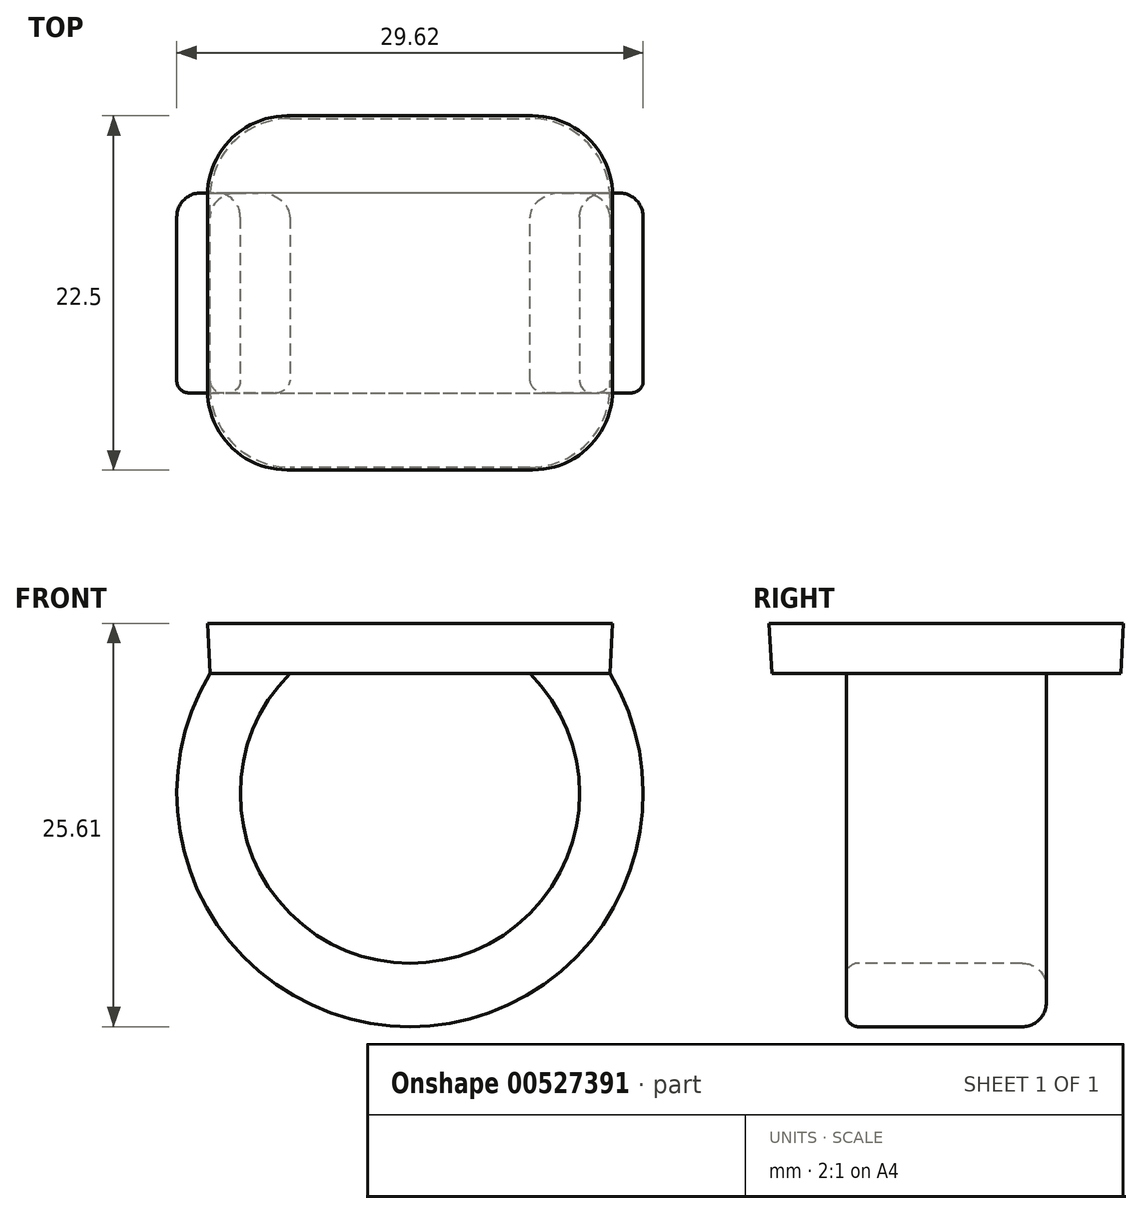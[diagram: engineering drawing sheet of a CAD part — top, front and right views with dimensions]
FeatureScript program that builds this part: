
annotation { "Feature Type Name" : "Feature", "Feature Type Description" : "" }
export const myFeature = defineFeature(function(context is Context, id is Id, definition is map)
    precondition{}
    {
        {
            var Q0;
            Q0=qCreatedBy(makeId("Top.planeOp"),FACE);
            var sketch = newSketch(context, id + "F0", { "sketchPlane" : qUnion([Q0])});
            skLineSegment(sketch, "E0.bottom", {"start": v(-12.7, 11.08) * mm, "end": v(12.7, 11.08) * mm});
            skLineSegment(sketch, "E0.top", {"start": v(-12.7, -11.08) * mm, "end": v(12.7, -11.08) * mm});
            skLineSegment(sketch, "E0.left", {"start": v(-12.7, 11.08) * mm, "end": v(-12.7, -11.08) * mm});
            skLineSegment(sketch, "E0.right", {"start": v(12.7, 11.08) * mm, "end": v(12.7, -11.08) * mm});
            skPoint(sketch, "E0.middle", {"position": v(0, 0) * mm});
            skLineSegment(sketch, "E1.left", {"start": v(23.14, -11.08) * mm, "end": v(23.14, -11.08) * mm});
            skLineSegment(sketch, "E1.right", {"start": v(2.26, -11.08) * mm, "end": v(2.26, -11.08) * mm});
            skPoint(sketch, "E1.middle", {"position": v(12.7, -11.08) * mm});
            skSolve(sketch);
        }
        {
            var Q0;
            Q0 = qSketchRegion(id + "F0", true);
            extrude(context, id + "F1", {"entities" : qUnion([Q0]), "depth" : 3.17 * mm, "offsetDistance" : 25.4 * mm, "hasDraft" : true, "draftAngle" : 3 * degree});
        }
        {
            var Q0;
            Q0=qCreatedBy(makeId("Front.planeOp"),FACE);
            var sketch = newSketch(context, id + "F2", { "sketchPlane" : qUnion([Q0])});
            skArc(sketch, "E2", {"start": v(-10.16, 0) * mm, "mid": v(0, -20.32) * mm, "end": v(10.16, 0) * mm});
            skSolve(sketch);
        }
        {
            var Q0;
            Q0=makeQuery(id+"F1.opExtrude","CAP_FACE",FACE,{"disambiguationData":[OSD([sQuery(id+"F0.wireOp",EDGE,"E0.bottom"),sQuery(id+"F0.wireOp",EDGE,"E0.top"),sQuery(id+"F0.wireOp",EDGE,"E0.left"),sQuery(id+"F0.wireOp",EDGE,"E0.right")])],"isStart":true});
            var sketch = newSketch(context, id + "F3", { "sketchPlane" : qUnion([Q0])});
            skLineSegment(sketch, "E3.bottom", {"start": v(-7.62, -6.35) * mm, "end": v(-12.7, -6.35) * mm});
            skLineSegment(sketch, "E3.top", {"start": v(-7.62, 6.35) * mm, "end": v(-12.7, 6.35) * mm});
            skLineSegment(sketch, "E3.left", {"start": v(-7.62, -6.35) * mm, "end": v(-7.62, 6.35) * mm});
            skLineSegment(sketch, "E3.right", {"start": v(-12.7, -6.35) * mm, "end": v(-12.7, 6.35) * mm});
            skPoint(sketch, "E3.middle", {"position": v(-10.16, 0) * mm});
            skSolve(sketch);
        }
        {
            var Q0;
            Q0 = qSketchRegion(id + "F3", true);
            var Q1;
            Q1 = qConstructionFilter(qBodyType(qCreatedBy(id + "F2" ,EDGE), BodyType.WIRE), ConstructionObject.NO);
            sweep(context, id + "F4", {"operationType" : NewBodyOperationType.ADD, "profiles" : qUnion([Q0]), "path" : qUnion([Q1])});
        }
        {
            var Q0;
            Q0=qCreatedBy(makeId("Front.planeOp"),FACE);
            var sketch = newSketch(context, id + "F5", { "sketchPlane" : qUnion([Q0])});
            skLineSegment(sketch, "E4.1", {"start": v(9.45, -2.44) * mm, "end": v(10.16, 0) * mm});
            skArc(sketch, "E4.2", {"start": v(9.45, -2.44) * mm, "mid": v(8.62, -1.15) * mm, "end": v(7.62, 0) * mm});
            skLineSegment(sketch, "E5.trimOffspring", {"start": v(7.62, 0) * mm, "end": v(10.16, 0) * mm});
            skPoint(sketch, "E4.0.start.orphan", {"position": v(-12.7, 0) * mm});
            skPoint(sketch, "E6.orphan", {"position": v(-7.62, 0) * mm});
            skPoint(sketch, "E7.orphan", {"position": v(12.7, 0) * mm});
            skSolve(sketch);
        }
        {
            var Q0;
            Q0 = qSketchRegion(id + "F5", true);
            var Q1;
            Q1=makeQuery(id+"F4.opSweep","SWEPT_FACE",FACE,{"disambiguationData":[OSD([sQuery(id+"F2.wireOp",EDGE,"E2"),sQuery(id+"F3.wireOp",EDGE,"E3.top")])]});
            var Q2;
            Q2=makeQuery(id+"F4.opSweep","SWEPT_FACE",FACE,{"disambiguationData":[OSD([sQuery(id+"F2.wireOp",EDGE,"E2"),sQuery(id+"F3.wireOp",EDGE,"E3.bottom")])]});
            extrude(context, id + "F6", {"entities" : qUnion([Q0]), "operationType" : NewBodyOperationType.ADD, "endBound" : BoundingType.UP_TO_SURFACE, "depth" : 25.4 * mm, "endBoundEntityFace" : qUnion([Q1]), "offsetDistance" : 25.4 * mm, "hasSecondDirection" : true, "secondDirectionBound" : SecondDirectionBoundingType.UP_TO_SURFACE, "secondDirectionOppositeDirection" : true, "secondDirectionDepth" : 25.4 * mm, "secondDirectionBoundEntityFace" : qUnion([Q2])});
        }
        {
            var Q0;
            Q0=makeQuery(id+"F1.opExtrude","SWEPT_EDGE",EDGE,{"disambiguationData":[OSD([sQuery(id+"F0.wireOp",EDGE,"E0.top"),sQuery(id+"F0.wireOp",EDGE,"E0.right")])]});
            var Q1;
            Q1=makeQuery(id+"F1.opExtrude","SWEPT_EDGE",EDGE,{"disambiguationData":[OSD([sQuery(id+"F0.wireOp",EDGE,"E0.bottom"),sQuery(id+"F0.wireOp",EDGE,"E0.right")])]});
            var Q2;
            Q2=makeQuery(id+"F1.opExtrude","SWEPT_EDGE",EDGE,{"disambiguationData":[OSD([sQuery(id+"F0.wireOp",EDGE,"E0.top"),sQuery(id+"F0.wireOp",EDGE,"E0.left")])]});
            var Q3;
            Q3=makeQuery(id+"F1.opExtrude","SWEPT_EDGE",EDGE,{"disambiguationData":[OSD([sQuery(id+"F0.wireOp",EDGE,"E0.bottom"),sQuery(id+"F0.wireOp",EDGE,"E0.left")])]});
            fillet(context, id + "F7", {"entities" : qUnion([Q0, Q1, Q2, Q3]), "radius" : 5.08 * mm, "tangentPropagation" : true, "allowEdgeOverflow" : false});
        }
        {
            var Q0;
            Q0=makeQuery(id+"F4.opSweep","SWEPT_EDGE",EDGE,{"disambiguationData":[OSD([sQuery(id+"F0.wireOp",EDGE,"E0.left"),sQuery(id+"F2.wireOp",EDGE,"E2"),sQuery(id+"F3.wireOp",EDGE,"E3.bottom"),sQuery(id+"F3.wireOp",EDGE,"E3.right")])]});
            var Q1;
            {var subQ0=sQuery(id+"F3.wireOp",EDGE,"E3.bottom");var subQ1=sQuery(id+"F2.wireOp",EDGE,"E2");Q1=makeQuery(id+"F6.boolean.opBoolean","MERGE",EDGE,{"derivedFrom":[makeQuery(id+"F4.opSweep","SWEPT_EDGE",EDGE,{"disambiguationData":[OSD([subQ1,subQ0,sQuery(id+"F3.wireOp",EDGE,"E3.left")])]}),makeQuery(id+"F6.opExtrude","TWEAK_EDGE",EDGE,{"derivedFrom":[makeQuery(id+"F4.opSweep","SWEPT_FACE",FACE,{"disambiguationData":[OSD([subQ1,subQ0])]}),makeQuery(id+"F5.imprint","IMPRINT",EDGE,{"derivedFrom":sQuery(id+"F5.wireOp",EDGE,"E4.2")})]})]});}
            fillet(context, id + "F8", {"entities" : qUnion([Q0, Q1]), "radius" : 1.52 * mm, "tangentPropagation" : true, "allowEdgeOverflow" : false});
        }
        {
            var Q0;
            {var subQ0=sQuery(id+"F3.wireOp",EDGE,"E3.top");var subQ1=sQuery(id+"F2.wireOp",EDGE,"E2");Q0=makeQuery(id+"F6.boolean.opBoolean","MERGE",EDGE,{"derivedFrom":[makeQuery(id+"F4.opSweep","SWEPT_EDGE",EDGE,{"disambiguationData":[OSD([subQ1,subQ0,sQuery(id+"F3.wireOp",EDGE,"E3.left")])]}),makeQuery(id+"F6.opExtrude","TWEAK_EDGE",EDGE,{"derivedFrom":[makeQuery(id+"F4.opSweep","SWEPT_FACE",FACE,{"disambiguationData":[OSD([subQ1,subQ0])]}),makeQuery(id+"F5.imprint","IMPRINT",EDGE,{"derivedFrom":sQuery(id+"F5.wireOp",EDGE,"E4.2")})]})]});}
            var Q1;
            Q1=makeQuery(id+"F4.opSweep","SWEPT_EDGE",EDGE,{"disambiguationData":[OSD([sQuery(id+"F0.wireOp",EDGE,"E0.left"),sQuery(id+"F2.wireOp",EDGE,"E2"),sQuery(id+"F3.wireOp",EDGE,"E3.top"),sQuery(id+"F3.wireOp",EDGE,"E3.right")])]});
            fillet(context, id + "F9", {"entities" : qUnion([Q0, Q1]), "radius" : 0.76 * mm, "tangentPropagation" : true, "allowEdgeOverflow" : false});
        }
    });
